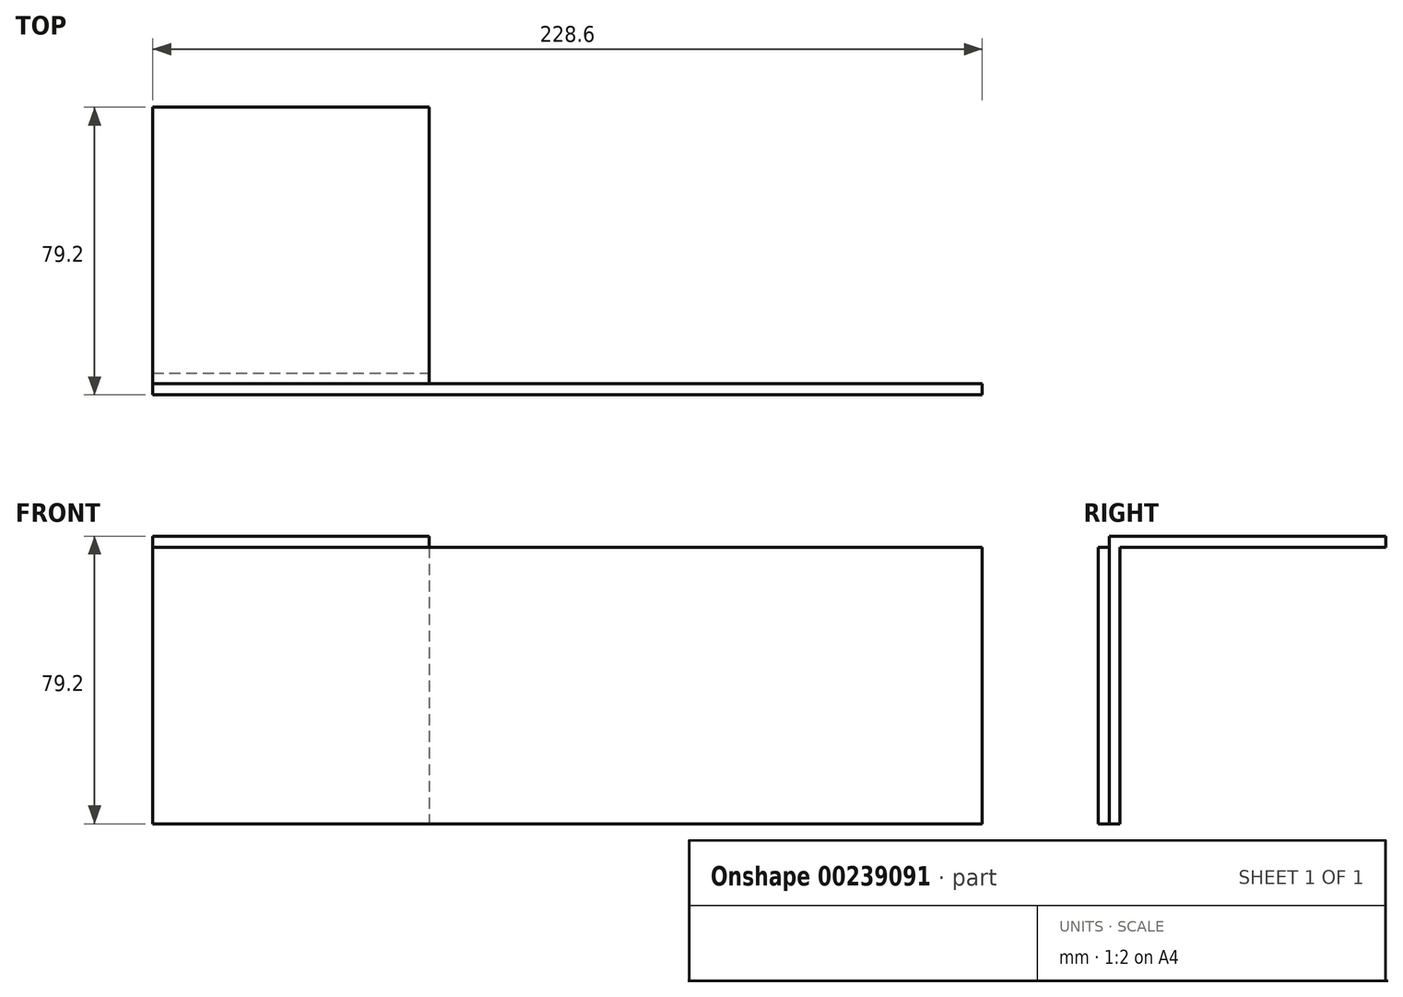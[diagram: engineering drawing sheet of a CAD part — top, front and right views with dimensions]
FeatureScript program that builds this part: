
annotation { "Feature Type Name" : "Feature", "Feature Type Description" : "" }
export const myFeature = defineFeature(function(context is Context, id is Id, definition is map)
    precondition{}
    {
        {
            assignVariable(context, id + "F0", {"name" : "v", "anyValue" : 3});
        }
        {
            var Q0;
            Q0=qCreatedBy(makeId("Front.planeOp"),FACE);
            var sketch = newSketch(context, id + "F1", { "sketchPlane" : qUnion([Q0])});
            skLineSegment(sketch, "E0.bottom", {"start": v(-114.3, 38.1) * mm, "end": v(114.3, 38.1) * mm});
            skLineSegment(sketch, "E0.top", {"start": v(-114.3, -38.1) * mm, "end": v(114.3, -38.1) * mm});
            skLineSegment(sketch, "E0.left", {"start": v(-114.3, 38.1) * mm, "end": v(-114.3, -38.1) * mm});
            skLineSegment(sketch, "E0.right", {"start": v(114.3, 38.1) * mm, "end": v(114.3, -38.1) * mm});
            skPoint(sketch, "E0.middle", {"position": v(0, 0) * mm});
            skSolve(sketch);
        }
        {
            var Q0;
            Q0 = qSketchRegion(id + "F1", true);
            extrude(context, id + "F2", {"entities" : qUnion([Q0]), "depth" : (getVariable(context, 'v')) * mm});
        }
        {
            var Q0;
            Q0=makeQuery(id+"F2.opExtrude","CAP_FACE",FACE,{"disambiguationData":[OSD([sQuery(id+"F1.wireOp",EDGE,"E0.bottom"),sQuery(id+"F1.wireOp",EDGE,"E0.top"),sQuery(id+"F1.wireOp",EDGE,"E0.left"),sQuery(id+"F1.wireOp",EDGE,"E0.right")])],"isStart":true});
            var sketch = newSketch(context, id + "F3", { "sketchPlane" : qUnion([Q0])});
            skLineSegment(sketch, "E1.bottom", {"start": v(114.3, 38.1) * mm, "end": v(38.1, 38.1) * mm});
            skLineSegment(sketch, "E1.top", {"start": v(114.3, -38.1) * mm, "end": v(38.1, -38.1) * mm});
            skLineSegment(sketch, "E1.left", {"start": v(114.3, 38.1) * mm, "end": v(114.3, -38.1) * mm});
            skLineSegment(sketch, "E1.right", {"start": v(38.1, 38.1) * mm, "end": v(38.1, -38.1) * mm});
            skSolve(sketch);
        }
        {
            var Q0;
            Q0 = qSketchRegion(id + "F3", true);
            extrude(context, id + "F4", {"entities" : qUnion([Q0]), "operationType" : NewBodyOperationType.ADD, "depth" : (getVariable(context, 'v')) * mm});
        }
        {
            var Q0;
            Q0=makeQuery(id+"F4.boolean.opBoolean","MERGE",FACE,{"derivedFrom":[makeQuery(id+"F2.opExtrude","SWEPT_FACE",FACE,{"disambiguationData":[OSD([sQuery(id+"F1.wireOp",EDGE,"E0.bottom")])]}),makeQuery(id+"F4.opExtrude","SWEPT_FACE",FACE,{"disambiguationData":[OSD([sQuery(id+"F3.wireOp",EDGE,"E1.bottom")])]})]});
            var sketch = newSketch(context, id + "F5", { "sketchPlane" : qUnion([Q0])});
            skLineSegment(sketch, "E2.bottom", {"start": v(-114.3, 76.2) * mm, "end": v(-38.1, 76.2) * mm});
            skLineSegment(sketch, "E2.top", {"start": v(-114.3, 0) * mm, "end": v(-38.1, 0) * mm});
            skLineSegment(sketch, "E2.left", {"start": v(-114.3, 76.2) * mm, "end": v(-114.3, 0) * mm});
            skLineSegment(sketch, "E2.right", {"start": v(-38.1, 76.2) * mm, "end": v(-38.1, 0) * mm});
            skSolve(sketch);
        }
        {
            var Q0;
            Q0 = qSketchRegion(id + "F5", true);
            extrude(context, id + "F6", {"entities" : qUnion([Q0]), "operationType" : NewBodyOperationType.ADD, "depth" : (getVariable(context, 'v')) * mm});
        }
    });
